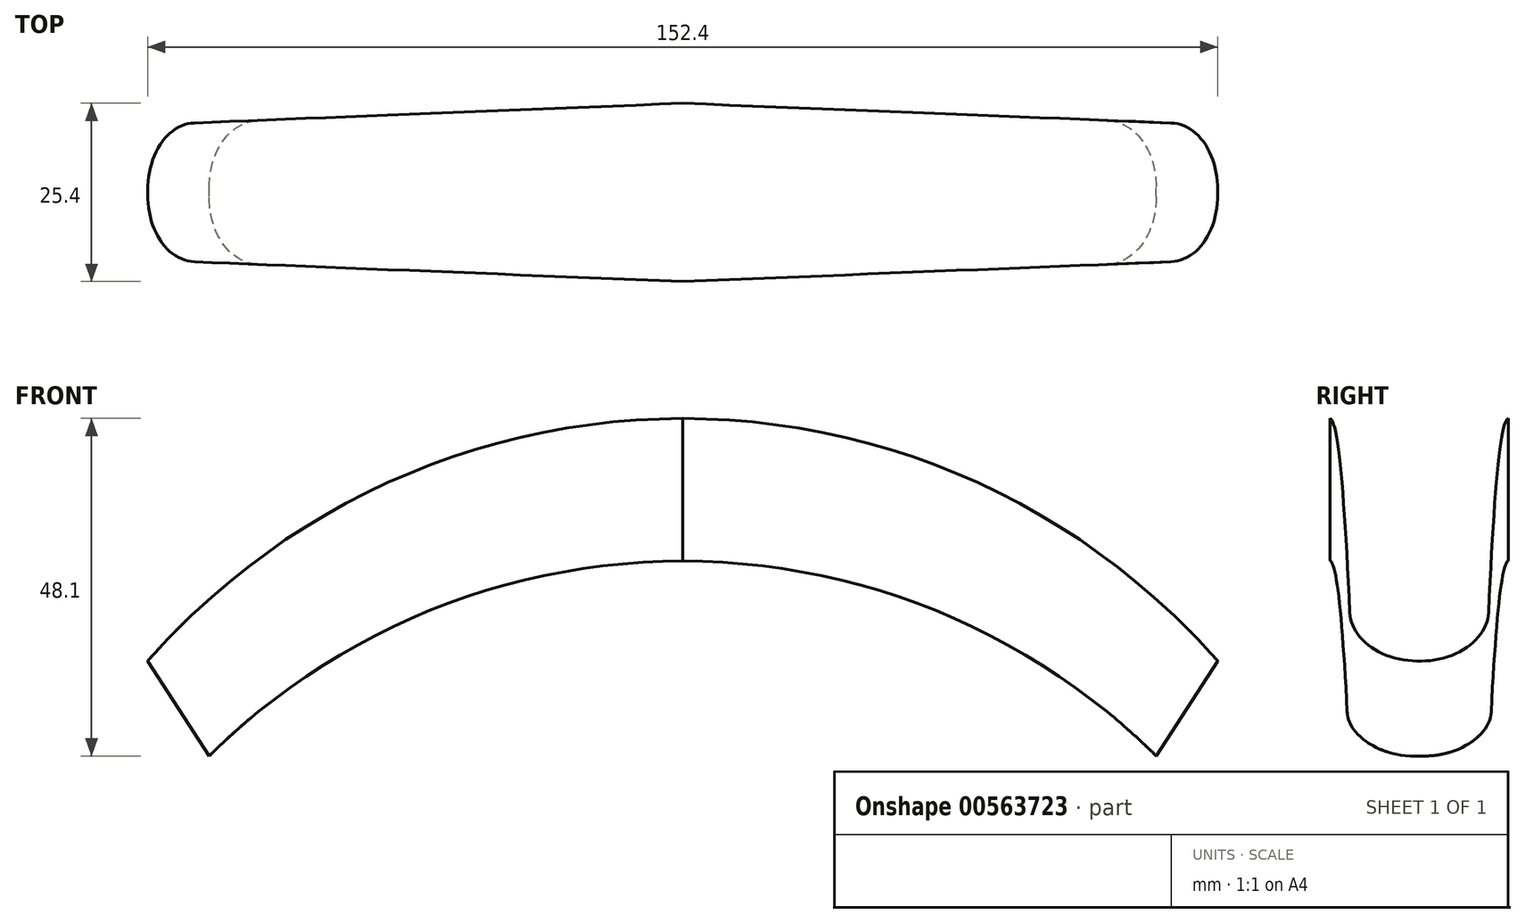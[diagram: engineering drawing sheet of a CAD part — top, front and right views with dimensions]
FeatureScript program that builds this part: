
annotation { "Feature Type Name" : "Feature", "Feature Type Description" : "" }
export const myFeature = defineFeature(function(context is Context, id is Id, definition is map)
    precondition{}
    {
        {
            var Q0;
            Q0=qCreatedBy(makeId("Front.planeOp"),FACE);
            var sketch = newSketch(context, id + "F0", { "sketchPlane" : qUnion([Q0])});
            skLineSegment(sketch, "E0", {"start": v(0, -2.31) * mm, "end": v(0, -18.19) * mm});
            skSolve(sketch);
        }
        {
            var Q0;
            Q0=qCreatedBy(makeId("Front.planeOp"),FACE);
            var sketch = newSketch(context, id + "F1", { "sketchPlane" : qUnion([Q0])});
            skArc(sketch, "E1", {"start": v(0, -1.84) * mm, "mid": v(-41.84, -10.89) * mm, "end": v(-76.2, -36.4) * mm});
            skArc(sketch, "E2", {"start": v(0, -22.16) * mm, "mid": v(-36.48, -29.38) * mm, "end": v(-67.46, -49.94) * mm});
            skLineSegment(sketch, "E3", {"start": v(-76.2, -36.4) * mm, "end": v(-67.46, -49.94) * mm});
            skArc(sketch, "E4.MirrorCS", {"start": v(0, -1.84) * mm, "mid": v(41.84, -10.89) * mm, "end": v(76.2, -36.4) * mm});
            skArc(sketch, "E5.MirrorCS", {"start": v(0, -22.16) * mm, "mid": v(36.48, -29.38) * mm, "end": v(67.46, -49.94) * mm});
            skLineSegment(sketch, "E6.MirrorCS", {"start": v(76.2, -36.4) * mm, "end": v(67.46, -49.94) * mm});
            skSolve(sketch);
        }
        {
            var Q0;
            Q0 = qSketchRegion(id + "F1", true);
            extrude(context, id + "F2", {"entities" : qUnion([Q0]), "endBound" : BoundingType.SYMMETRIC, "depth" : 25.4 * mm, "offsetDistance" : 25.4 * mm});
        }
        {
            var Q0;
            Q0=qCreatedBy(makeId("Top.planeOp"),FACE);
            var sketch = newSketch(context, id + "F3", { "sketchPlane" : qUnion([Q0])});
            skLineSegment(sketch, "E7", {"start": v(0, 12.7) * mm, "end": v(-77.08, 9.59) * mm});
            skLineSegment(sketch, "E8", {"start": v(-77.08, 9.59) * mm, "end": v(-77.2, 12.7) * mm});
            skLineSegment(sketch, "E9", {"start": v(-77.2, 12.7) * mm, "end": v(0, 12.7) * mm});
            skLineSegment(sketch, "E10.MirrorCS", {"start": v(0, -12.7) * mm, "end": v(-77.08, -9.59) * mm});
            skLineSegment(sketch, "E11.MirrorCS", {"start": v(-77.2, -12.7) * mm, "end": v(0, -12.7) * mm});
            skLineSegment(sketch, "E12.MirrorCS", {"start": v(-77.08, -9.59) * mm, "end": v(-77.2, -12.7) * mm});
            skLineSegment(sketch, "E13.MirrorCS", {"start": v(77.2, 12.7) * mm, "end": v(0, 12.7) * mm});
            skLineSegment(sketch, "E14.MirrorCS", {"start": v(0, 12.7) * mm, "end": v(77.08, 9.59) * mm});
            skLineSegment(sketch, "E15.MirrorCS", {"start": v(77.08, 9.59) * mm, "end": v(77.2, 12.7) * mm});
            skLineSegment(sketch, "E16.MirrorCS", {"start": v(0, -12.7) * mm, "end": v(77.08, -9.59) * mm});
            skLineSegment(sketch, "E17.MirrorCS", {"start": v(77.2, -12.7) * mm, "end": v(0, -12.7) * mm});
            skLineSegment(sketch, "E18.MirrorCS", {"start": v(77.08, -9.59) * mm, "end": v(77.2, -12.7) * mm});
            skSolve(sketch);
        }
        {
            var Q0;
            Q0 = qSketchRegion(id + "F3", true);
            extrude(context, id + "F4", {"entities" : qUnion([Q0]), "operationType" : NewBodyOperationType.REMOVE, "oppositeDirection" : true, "depth" : 127 * mm, "offsetDistance" : 25.4 * mm});
        }
        {
            var Q0;
            Q0=makeQuery(id+"F4.boolean.opBoolean","INTERSECT",EDGE,{"derivedFrom":[makeQuery(id+"F2.opExtrude","SWEPT_FACE",FACE,{"disambiguationData":[OSD([sQuery(id+"F1.wireOp",EDGE,"E3")])]}),makeQuery(id+"F4.opExtrude","SWEPT_FACE",FACE,{"disambiguationData":[OSD([sQuery(id+"F3.wireOp",EDGE,"E10.MirrorCS")])]})]});
            var Q1;
            Q1=makeQuery(id+"F4.boolean.opBoolean","INTERSECT",EDGE,{"derivedFrom":[makeQuery(id+"F2.opExtrude","SWEPT_FACE",FACE,{"disambiguationData":[OSD([sQuery(id+"F1.wireOp",EDGE,"E3")])]}),makeQuery(id+"F4.opExtrude","SWEPT_FACE",FACE,{"disambiguationData":[OSD([sQuery(id+"F3.wireOp",EDGE,"E7")])]})]});
            var Q2;
            Q2=makeQuery(id+"F4.boolean.opBoolean","INTERSECT",EDGE,{"derivedFrom":[makeQuery(id+"F2.opExtrude","SWEPT_FACE",FACE,{"disambiguationData":[OSD([sQuery(id+"F1.wireOp",EDGE,"E6.MirrorCS")])]}),makeQuery(id+"F4.opExtrude","SWEPT_FACE",FACE,{"disambiguationData":[OSD([sQuery(id+"F3.wireOp",EDGE,"E16.MirrorCS")])]})]});
            var Q3;
            Q3=makeQuery(id+"F4.boolean.opBoolean","INTERSECT",EDGE,{"derivedFrom":[makeQuery(id+"F2.opExtrude","SWEPT_FACE",FACE,{"disambiguationData":[OSD([sQuery(id+"F1.wireOp",EDGE,"E6.MirrorCS")])]}),makeQuery(id+"F4.opExtrude","SWEPT_FACE",FACE,{"disambiguationData":[OSD([sQuery(id+"F3.wireOp",EDGE,"E14.MirrorCS")])]})]});
            fillet(context, id + "F5", {"entities" : qUnion([Q0, Q1, Q2, Q3]), "radius" : 9.65 * mm, "tangentPropagation" : true, "allowEdgeOverflow" : false});
        }
    });
